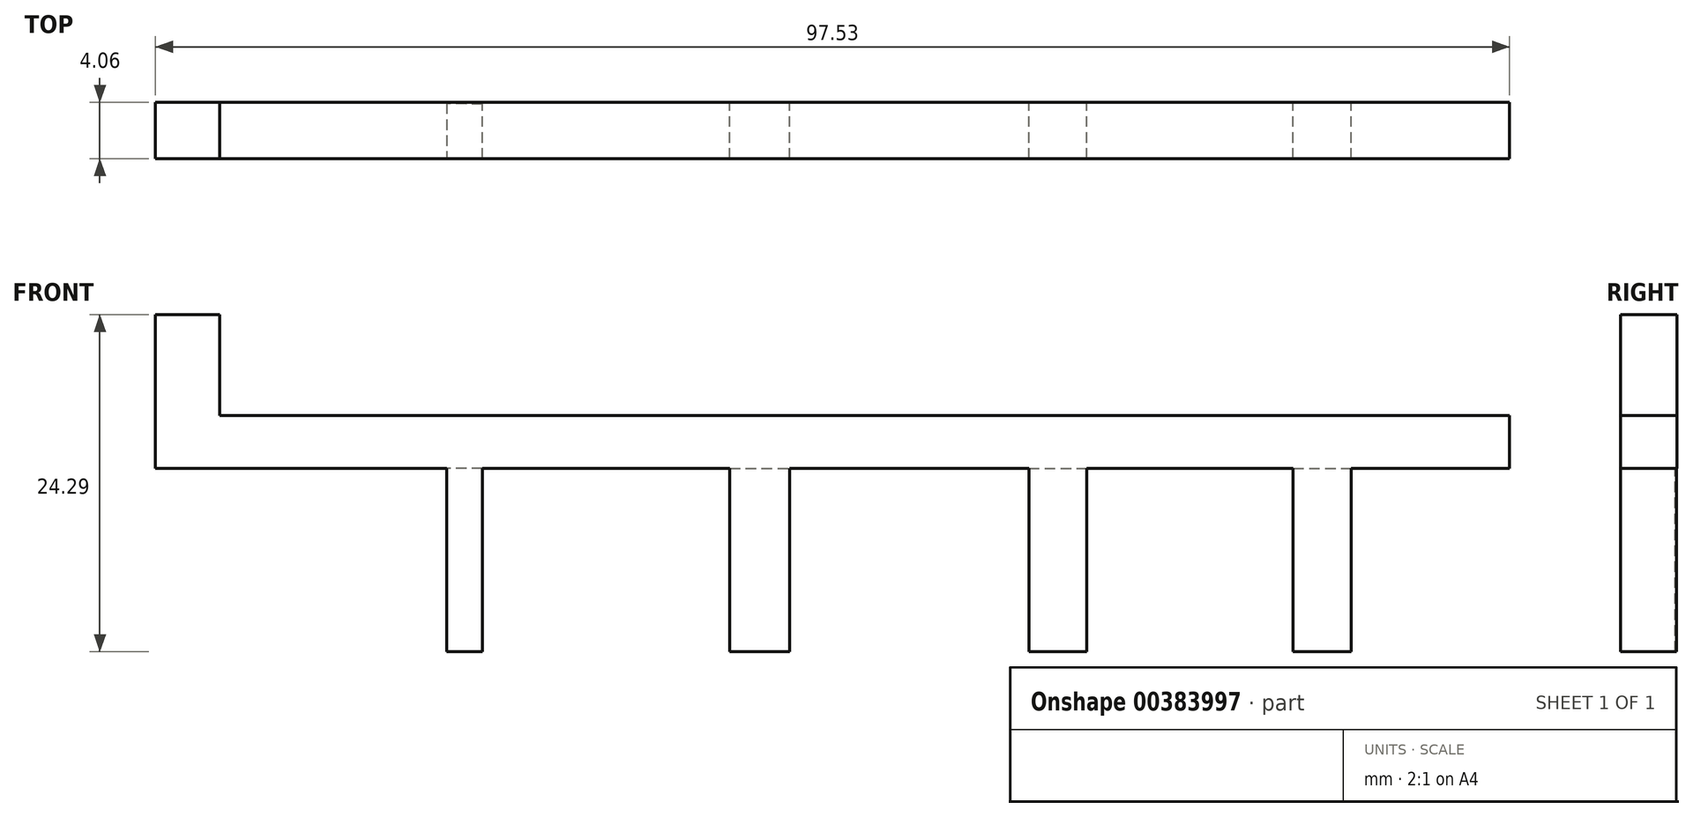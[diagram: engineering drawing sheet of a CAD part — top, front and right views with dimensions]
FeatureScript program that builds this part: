
annotation { "Feature Type Name" : "Feature", "Feature Type Description" : "" }
export const myFeature = defineFeature(function(context is Context, id is Id, definition is map)
    precondition{}
    {
        {
            var Q0;
            Q0=qCreatedBy(makeId("Front.planeOp"),FACE);
            var sketch = newSketch(context, id + "F0", { "sketchPlane" : qUnion([Q0])});
            skLineSegment(sketch, "E0", {"start": v(45.8, 0) * mm, "end": v(45.8, 3.8) * mm});
            skLineSegment(sketch, "E1", {"start": v(45.8, 3.8) * mm, "end": v(0, 3.8) * mm});
            skLineSegment(sketch, "E2", {"start": v(0, 3.8) * mm, "end": v(0, 0) * mm});
            skLineSegment(sketch, "E3", {"start": v(0, 0) * mm, "end": v(45.8, 0) * mm});
            skLineSegment(sketch, "E4", {"start": v(0, 3.8) * mm, "end": v(-51.74, 3.8) * mm});
            skLineSegment(sketch, "E5", {"start": v(-51.74, 3.8) * mm, "end": v(-51.74, 0) * mm});
            skLineSegment(sketch, "E6", {"start": v(-51.74, 0) * mm, "end": v(0, 0) * mm});
            skLineSegment(sketch, "E7", {"start": v(-51.74, 3.8) * mm, "end": v(-51.74, 11.08) * mm});
            skLineSegment(sketch, "E8", {"start": v(-47.11, 11.08) * mm, "end": v(-47.11, 3.8) * mm});
            skLineSegment(sketch, "E9", {"start": v(-47.11, 3.8) * mm, "end": v(-47.11, 11.08) * mm});
            skLineSegment(sketch, "E10", {"start": v(-51.74, 11.08) * mm, "end": v(-47.11, 11.08) * mm});
            skSolve(sketch);
        }
        {
            var Q0;
            {var subQ0=sQuery(id+"F0.wireOp",EDGE,"E7");Q0=makeQuery(id+"F0.imprint","IMPRINT",FACE,{"disambiguationData":[TD([[makeQuery(id+"F0.imprint","IMPRINT",EDGE,{"derivedFrom":subQ0}),-1.0]])]});}
            var Q1;
            {var subQ3=sQuery(id+"F0.wireOp",EDGE,"E2");Q1=makeQuery(id+"F0.imprint","IMPRINT",FACE,{"disambiguationData":[TD([[makeQuery(id+"F0.imprint","IMPRINT",EDGE,{"derivedFrom":subQ3}),-1.0]])]});}
            var Q2;
            Q2=makeQuery(id+"F0.imprint","IMPRINT",FACE,{"disambiguationData":[TD([[makeQuery(id+"F0.imprint","IMPRINT",EDGE,{"derivedFrom":sQuery(id+"F0.wireOp",EDGE,"E0")}),1.0]])]});
            extrude(context, id + "F1", {"entities" : qUnion([Q0, Q1, Q2]), "oppositeDirection" : true, "depth" : 4.06 * mm, "offsetDistance" : 25.4 * mm});
        }
        {
            var Q0;
            Q0=qCreatedBy(makeId("Top.planeOp"),FACE);
            var sketch = newSketch(context, id + "F2", { "sketchPlane" : qUnion([Q0])});
            skLineSegment(sketch, "E11", {"start": v(-30.75, 3.97) * mm, "end": v(-30.75, 0) * mm});
            skLineSegment(sketch, "E12", {"start": v(-30.75, 0) * mm, "end": v(-28.2, 0) * mm});
            skLineSegment(sketch, "E13", {"start": v(-28.2, 0) * mm, "end": v(-28.2, 3.92) * mm});
            skLineSegment(sketch, "E14", {"start": v(-28.2, 3.92) * mm, "end": v(-30.75, 3.97) * mm});
            skLineSegment(sketch, "E15.bottom", {"start": v(-10.38, 0) * mm, "end": v(-6.07, 0) * mm});
            skLineSegment(sketch, "E15.top", {"start": v(-10.38, 4.04) * mm, "end": v(-6.07, 4.04) * mm});
            skLineSegment(sketch, "E15.left", {"start": v(-10.38, 0) * mm, "end": v(-10.38, 4.04) * mm});
            skLineSegment(sketch, "E15.right", {"start": v(-6.07, 0) * mm, "end": v(-6.07, 4.04) * mm});
            skLineSegment(sketch, "E16.bottom", {"start": v(11.16, 0) * mm, "end": v(15.33, 0) * mm});
            skLineSegment(sketch, "E16.top", {"start": v(11.16, 4.04) * mm, "end": v(15.33, 4.04) * mm});
            skLineSegment(sketch, "E16.left", {"start": v(11.16, 0) * mm, "end": v(11.16, 4.04) * mm});
            skLineSegment(sketch, "E16.right", {"start": v(15.33, 0) * mm, "end": v(15.33, 4.04) * mm});
            skLineSegment(sketch, "E17.bottom", {"start": v(30.2, 0) * mm, "end": v(34.38, 0) * mm});
            skLineSegment(sketch, "E17.top", {"start": v(30.2, 4.04) * mm, "end": v(34.38, 4.04) * mm});
            skLineSegment(sketch, "E17.left", {"start": v(30.2, 0) * mm, "end": v(30.2, 4.04) * mm});
            skLineSegment(sketch, "E17.right", {"start": v(34.38, 0) * mm, "end": v(34.38, 4.04) * mm});
            skSolve(sketch);
        }
        {
            var Q0;
            Q0 = qSketchRegion(id + "F2", true);
            extrude(context, id + "F3", {"entities" : qUnion([Q0]), "operationType" : NewBodyOperationType.ADD, "oppositeDirection" : true, "depth" : 13.2 * mm, "offsetDistance" : 25.4 * mm});
        }
    });
